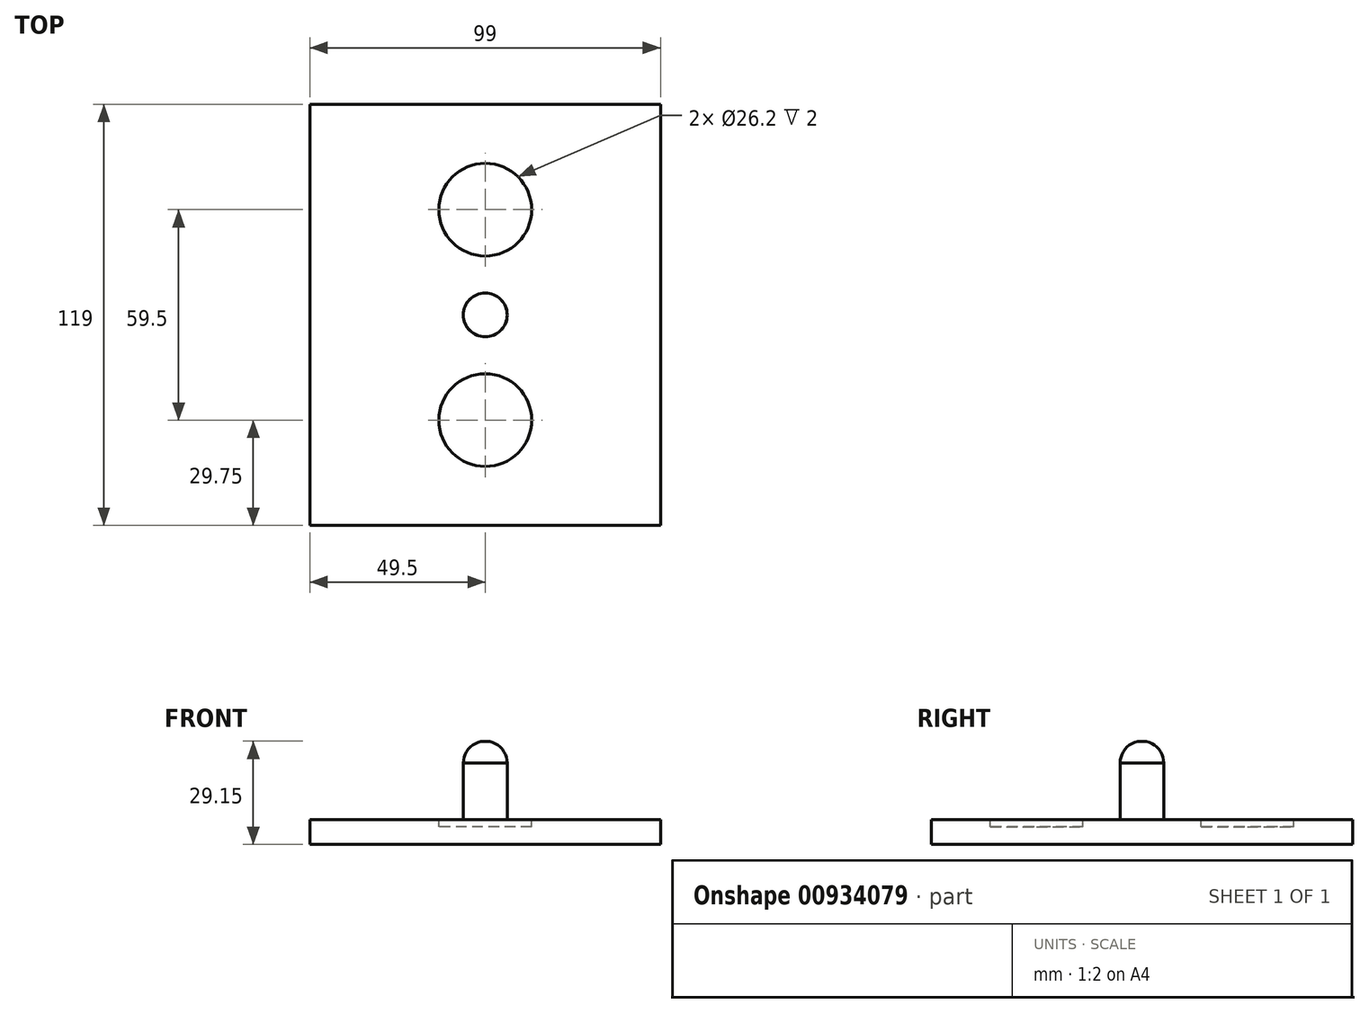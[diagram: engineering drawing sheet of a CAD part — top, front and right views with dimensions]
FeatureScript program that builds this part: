
annotation { "Feature Type Name" : "Feature", "Feature Type Description" : "" }
export const myFeature = defineFeature(function(context is Context, id is Id, definition is map)
    precondition{}
    {
        {
            var Q0;
            Q0=qCreatedBy(makeId("Top.planeOp"),FACE);
            var sketch = newSketch(context, id + "F0", { "sketchPlane" : qUnion([Q0])});
            skLineSegment(sketch, "E0.bottom", {"start": v(-49.5, 59.5) * mm, "end": v(49.5, 59.5) * mm});
            skLineSegment(sketch, "E0.top", {"start": v(-49.5, -59.5) * mm, "end": v(49.5, -59.5) * mm});
            skLineSegment(sketch, "E0.left", {"start": v(-49.5, 59.5) * mm, "end": v(-49.5, -59.5) * mm});
            skLineSegment(sketch, "E0.right", {"start": v(49.5, 59.5) * mm, "end": v(49.5, -59.5) * mm});
            skPoint(sketch, "E0.middle", {"position": v(0, 0) * mm});
            skSolve(sketch);
        }
        {
            var Q0;
            Q0=makeQuery(id+"F0.imprint","IMPRINT",FACE,{"disambiguationData":[TD([[makeQuery(id+"F0.imprint","IMPRINT",EDGE,{"derivedFrom":sQuery(id+"F0.wireOp",EDGE,"E0.bottom")}),-1.0]])]});
            extrude(context, id + "F1", {"entities" : qUnion([Q0]), "depth" : 7 * mm, "offsetDistance" : 25 * mm});
        }
        {
            var Q0;
            Q0=makeQuery(id+"F1.opExtrude","CAP_FACE",FACE,{"disambiguationData":[OSD([sQuery(id+"F0.wireOp",EDGE,"E0.bottom"),sQuery(id+"F0.wireOp",EDGE,"E0.top"),sQuery(id+"F0.wireOp",EDGE,"E0.left"),sQuery(id+"F0.wireOp",EDGE,"E0.right")])],"isStart":false});
            var sketch = newSketch(context, id + "F2", { "sketchPlane" : qUnion([Q0])});
            skCircle(sketch, "E1", {"center": v(0, 0) * mm, "radius": 6.2 * mm});
            skLineSegment(sketch, "E2", {"start": v(0, 0) * mm, "end": v(0, 59.5) * mm});
            skLineSegment(sketch, "E3", {"start": v(0, 59.5) * mm, "end": v(-0.5, 59.85) * mm});
            skCircle(sketch, "E4", {"center": v(0, 29.75) * mm, "radius": 13.1 * mm});
            skLineSegment(sketch, "E5", {"start": v(0, 0) * mm, "end": v(0, -59.5) * mm});
            skCircle(sketch, "E6", {"center": v(0, -29.75) * mm, "radius": 13.1 * mm});
            skSolve(sketch);
        }
        {
            var Q0;
            Q0=makeQuery(id+"F2.imprint","IMPRINT",FACE,{"disambiguationData":[TD([[makeQuery(id+"F2.imprint","IMPRINT",EDGE,{"derivedFrom":sQuery(id+"F2.wireOp",EDGE,"E1")}),1.0]])]});
            extrude(context, id + "F3", {"entities" : qUnion([Q0]), "operationType" : NewBodyOperationType.ADD, "depth" : 16 * mm, "offsetDistance" : 25 * mm});
        }
        {
            var Q0;
            {var subQ0=sQuery(id+"F2.wireOp",EDGE,"E4");var subQ1=sQuery(id+"F2.wireOp",EDGE,"E2");var subQ2=makeQuery(id+"F2.imprint","INTERSECT",VERTEX,{"disambiguationData":[OD(0.0)],"derivedFrom":[subQ1,subQ0]});Q0=makeQuery(id+"F2.imprint","IMPRINT",FACE,{"disambiguationData":[TD([[makeQuery(id+"F2.imprint","IMPRINT",EDGE,{"disambiguationData":[TD([[subQ2,-1.0]])],"derivedFrom":subQ1}),-1.0]])]});}
            var Q1;
            {var subQ0=sQuery(id+"F2.wireOp",EDGE,"E4");var subQ1=sQuery(id+"F2.wireOp",EDGE,"E2");var subQ2=makeQuery(id+"F2.imprint","INTERSECT",VERTEX,{"disambiguationData":[OD(0.0)],"derivedFrom":[subQ1,subQ0]});Q1=makeQuery(id+"F2.imprint","IMPRINT",FACE,{"disambiguationData":[TD([[makeQuery(id+"F2.imprint","IMPRINT",EDGE,{"disambiguationData":[TD([[subQ2,-1.0]])],"derivedFrom":subQ1}),1.0]])]});}
            var Q2;
            {var subQ0=sQuery(id+"F2.wireOp",EDGE,"E6");var subQ1=sQuery(id+"F2.wireOp",EDGE,"E5");var subQ2=makeQuery(id+"F2.imprint","INTERSECT",VERTEX,{"disambiguationData":[OD(0.0)],"derivedFrom":[subQ1,subQ0]});Q2=makeQuery(id+"F2.imprint","IMPRINT",FACE,{"disambiguationData":[TD([[makeQuery(id+"F2.imprint","IMPRINT",EDGE,{"disambiguationData":[TD([[subQ2,-1.0]])],"derivedFrom":subQ1}),1.0]])]});}
            var Q3;
            {var subQ0=sQuery(id+"F2.wireOp",EDGE,"E6");var subQ1=sQuery(id+"F2.wireOp",EDGE,"E5");var subQ2=makeQuery(id+"F2.imprint","INTERSECT",VERTEX,{"disambiguationData":[OD(0.0)],"derivedFrom":[subQ1,subQ0]});Q3=makeQuery(id+"F2.imprint","IMPRINT",FACE,{"disambiguationData":[TD([[makeQuery(id+"F2.imprint","IMPRINT",EDGE,{"disambiguationData":[TD([[subQ2,-1.0]])],"derivedFrom":subQ1}),-1.0]])]});}
            extrude(context, id + "F4", {"entities" : qUnion([Q0, Q1, Q2, Q3]), "operationType" : NewBodyOperationType.REMOVE, "oppositeDirection" : true, "depth" : 2 * mm, "offsetDistance" : 25 * mm});
        }
        {
            var Q0;
            Q0=makeQuery(id+"F3.opExtrude","CAP_FACE",FACE,{"disambiguationData":[OSD([sQuery(id+"F2.wireOp",EDGE,"E1")])],"isStart":false});
            var sketch = newSketch(context, id + "F5", { "sketchPlane" : qUnion([Q0])});
            skArc(sketch, "E7", {"start": v(6.2, 0) * mm, "mid": v(0, 6.15) * mm, "end": v(-6.2, 0) * mm});
            skLineSegment(sketch, "E8", {"start": v(-6.2, 0) * mm, "end": v(6.2, 0) * mm});
            skSolve(sketch);
        }
        {
            var Q0;
            Q0=makeQuery(id+"F5.imprint","IMPRINT",FACE,{"disambiguationData":[TD([[makeQuery(id+"F5.imprint","IMPRINT",EDGE,{"derivedFrom":sQuery(id+"F5.wireOp",EDGE,"E7")}),1.0]])]});
            var Q1;
            Q1=sQuery(id+"F5.wireOp",EDGE,"E8");
            revolve(context, id + "F6", {"operationType" : NewBodyOperationType.ADD, "surfaceOperationType" : NewSurfaceOperationType.NEW, "entities" : qUnion([Q0]), "axis" : qUnion([Q1]), "revolveType" : RevolveType.FULL});
        }
    });
